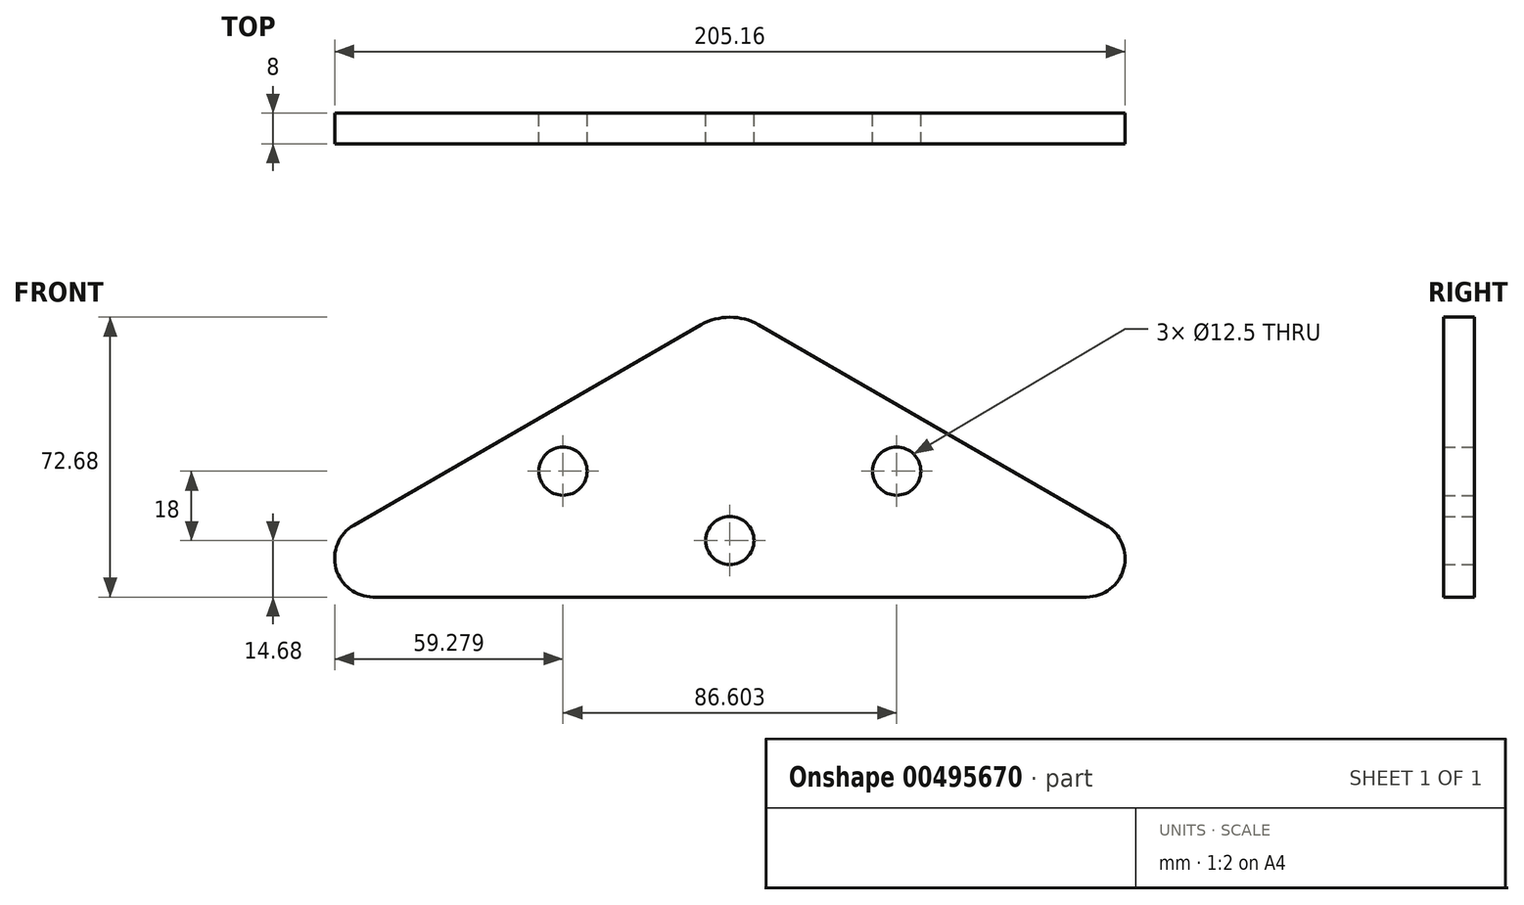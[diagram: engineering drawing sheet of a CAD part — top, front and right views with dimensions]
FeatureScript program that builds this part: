
annotation { "Feature Type Name" : "Feature", "Feature Type Description" : "" }
export const myFeature = defineFeature(function(context is Context, id is Id, definition is map)
    precondition{}
    {
        {
            var Q0;
            Q0=qCreatedBy(makeId("Front.planeOp"),FACE);
            var sketch = newSketch(context, id + "F0", { "sketchPlane" : qUnion([Q0])});
            skLineSegment(sketch, "E0", {"start": v(0, 0) * mm, "end": v(-92.58, 0) * mm});
            skLineSegment(sketch, "E1", {"start": v(-97.58, 18.66) * mm, "end": v(-7.5, 70.67) * mm});
            skLineSegment(sketch, "E2", {"start": v(0, 75) * mm, "end": v(0, 0) * mm, "construction": true});
            skCircle(sketch, "E3", {"center": v(-43.3, 32.68) * mm, "radius": 6.25 * mm});
            skLineSegment(sketch, "E4", {"start": v(-43.3, 32.68) * mm, "end": v(0, 57.68) * mm, "construction": true});
            skPoint(sketch, "E5.visualSharp", {"position": v(-129.9, 0) * mm});
            skArc(sketch, "E5.filletArc", {"start": v(-97.58, 18.66) * mm, "mid": v(-102.24, 7.41) * mm, "end": v(-92.58, 0) * mm});
            skLineSegment(sketch, "E6.MirrorCS", {"start": v(43.3, 32.68) * mm, "end": v(0, 57.68) * mm, "construction": true});
            skPoint(sketch, "E7.MirrorP", {"position": v(129.9, 0) * mm});
            skCircle(sketch, "E8.MirrorC", {"center": v(43.3, 32.68) * mm, "radius": 6.25 * mm});
            skArc(sketch, "E9.MirrorCS", {"start": v(97.58, 18.66) * mm, "mid": v(102.24, 7.41) * mm, "end": v(92.58, 0) * mm});
            skLineSegment(sketch, "E10.MirrorCS", {"start": v(97.58, 18.66) * mm, "end": v(7.5, 70.67) * mm});
            skLineSegment(sketch, "E11.MirrorCS", {"start": v(0, 0) * mm, "end": v(92.58, 0) * mm});
            skPoint(sketch, "E12.visualSharp", {"position": v(0, 75) * mm});
            skArc(sketch, "E12.filletArc", {"start": v(7.5, 70.67) * mm, "mid": v(0, 72.68) * mm, "end": v(-7.5, 70.67) * mm});
            skCircle(sketch, "E13", {"center": v(0, 14.68) * mm, "radius": 6.25 * mm});
            skSolve(sketch);
        }
        {
            var Q0;
            Q0 = qSketchRegion(id + "F0", true);
            extrude(context, id + "F1", {"entities" : qUnion([Q0]), "depth" : 8 * mm});
        }
    });
